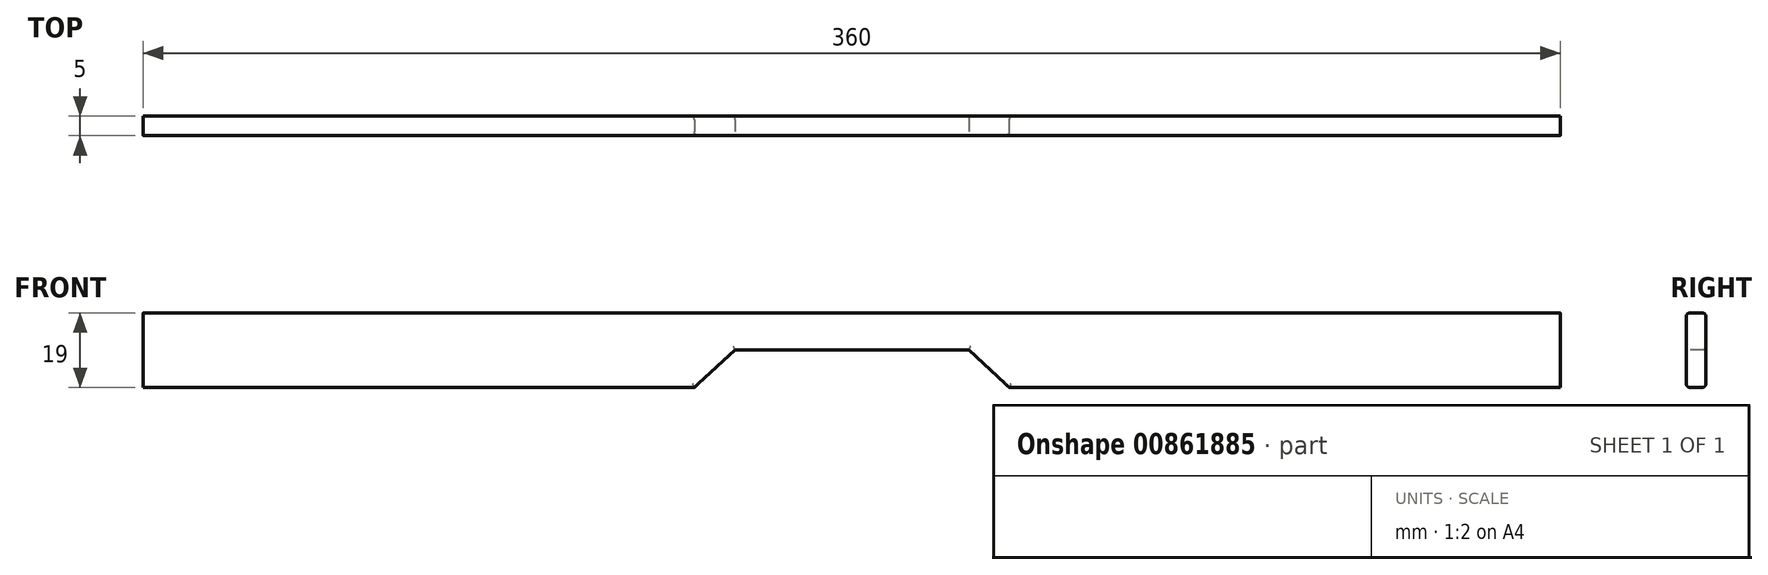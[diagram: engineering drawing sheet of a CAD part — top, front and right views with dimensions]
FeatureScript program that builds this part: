
annotation { "Feature Type Name" : "Feature", "Feature Type Description" : "" }
export const myFeature = defineFeature(function(context is Context, id is Id, definition is map)
    precondition{}
    {
        {
            var Q0;
            Q0=qCreatedBy(makeId("Front.planeOp"),FACE);
            var sketch = newSketch(context, id + "F0", { "sketchPlane" : qUnion([Q0])});
            skLineSegment(sketch, "E0.bottom", {"start": v(-180, 9.5) * mm, "end": v(180, 9.5) * mm});
            skLineSegment(sketch, "E0.top", {"start": v(-180, -9.5) * mm, "end": v(180, -9.5) * mm});
            skLineSegment(sketch, "E0.left", {"start": v(-180, 9.5) * mm, "end": v(-180, -9.5) * mm});
            skLineSegment(sketch, "E0.right", {"start": v(180, 9.5) * mm, "end": v(180, -9.5) * mm});
            skPoint(sketch, "E0.middle", {"position": v(0, 0) * mm});
            skSolve(sketch);
        }
        {
            var Q0;
            Q0=makeQuery(id+"F0.imprint","IMPRINT",FACE,{"disambiguationData":[TD([[makeQuery(id+"F0.imprint","IMPRINT",EDGE,{"derivedFrom":sQuery(id+"F0.wireOp",EDGE,"E0.bottom")}),-1.0]])]});
            extrude(context, id + "F1", {"entities" : qUnion([Q0]), "depth" : 5 * mm, "offsetDistance" : 25 * mm});
        }
        {
            var Q0;
            Q0=makeQuery(id+"F1.opExtrude","CAP_FACE",FACE,{"disambiguationData":[OSD([sQuery(id+"F0.wireOp",EDGE,"E0.bottom"),sQuery(id+"F0.wireOp",EDGE,"E0.top"),sQuery(id+"F0.wireOp",EDGE,"E0.left"),sQuery(id+"F0.wireOp",EDGE,"E0.right")])],"isStart":false});
            var sketch = newSketch(context, id + "F2", { "sketchPlane" : qUnion([Q0])});
            skLineSegment(sketch, "E1", {"start": v(-180, -9.5) * mm, "end": v(-40, -9.5) * mm});
            skLineSegment(sketch, "E2", {"start": v(180, -9.5) * mm, "end": v(40, -9.5) * mm});
            skLineSegment(sketch, "E3", {"start": v(-40, -9.5) * mm, "end": v(-29.72, 0) * mm});
            skLineSegment(sketch, "E4", {"start": v(-29.72, 0) * mm, "end": v(29.72, 0) * mm});
            skLineSegment(sketch, "E5", {"start": v(29.72, 0) * mm, "end": v(40, -9.5) * mm});
            skSolve(sketch);
        }
        {
            var Q0;
            Q0 = qSketchRegion(id + "F2", true);
            var Q1;
            {var subQ0=sQuery(id+"F2.wireOp",EDGE,"E3");Q1=makeQuery(id+"F2.imprint","IMPRINT",FACE,{"disambiguationData":[TD([[makeQuery(id+"F2.imprint","IMPRINT",EDGE,{"derivedFrom":subQ0}),-1.0]])]});}
            extrude(context, id + "F3", {"entities" : qUnion([Q0, Q1]), "operationType" : NewBodyOperationType.REMOVE, "oppositeDirection" : true, "depth" : 25 * mm, "offsetDistance" : 25 * mm});
        }
        {
            var Q0;
            Q0=makeQuery(id+"F1.opExtrude","CAP_EDGE",EDGE,{"disambiguationData":[OSD([sQuery(id+"F0.wireOp",EDGE,"E0.bottom")])],"isStart":false});
            var Q1;
            Q1=makeQuery(id+"F1.opExtrude","CAP_EDGE",EDGE,{"disambiguationData":[OSD([sQuery(id+"F0.wireOp",EDGE,"E0.bottom")])],"isStart":true});
            var Q2;
            {var subQ0=sQuery(id+"F0.wireOp",EDGE,"E0.left");var subQ1=sQuery(id+"F0.wireOp",EDGE,"E0.top");Q2=makeQuery(id+"F3.boolean.opBoolean","SPLIT",EDGE,{"disambiguationData":[TD([makeQuery(id+"F1.opExtrude","SWEPT_FACE",FACE,{"disambiguationData":[OSD([subQ0])]})])],"derivedFrom":makeQuery(id+"F1.opExtrude","CAP_EDGE",EDGE,{"disambiguationData":[OSD([subQ1])],"isStart":false})});}
            var Q3;
            {var subQ0=sQuery(id+"F0.wireOp",EDGE,"E0.right");var subQ1=sQuery(id+"F0.wireOp",EDGE,"E0.top");Q3=makeQuery(id+"F3.boolean.opBoolean","SPLIT",EDGE,{"disambiguationData":[TD([makeQuery(id+"F1.opExtrude","SWEPT_FACE",FACE,{"disambiguationData":[OSD([subQ0])]})])],"derivedFrom":makeQuery(id+"F1.opExtrude","CAP_EDGE",EDGE,{"disambiguationData":[OSD([subQ1])],"isStart":false})});}
            var Q4;
            Q4=makeQuery(id+"F3.boolean.opBoolean","COPY",EDGE,{"derivedFrom":makeQuery(id+"F3.opExtrude","CAP_EDGE",EDGE,{"disambiguationData":[OSD([sQuery(id+"F2.wireOp",EDGE,"E4")])],"isStart":true})});
            var Q5;
            Q5=makeQuery(id+"F3.boolean.opBoolean","COPY",EDGE,{"derivedFrom":makeQuery(id+"F3.opExtrude","CAP_EDGE",EDGE,{"disambiguationData":[OSD([sQuery(id+"F2.wireOp",EDGE,"E5")])],"isStart":true})});
            var Q6;
            Q6=makeQuery(id+"F3.boolean.opBoolean","COPY",EDGE,{"derivedFrom":makeQuery(id+"F3.opExtrude","CAP_EDGE",EDGE,{"disambiguationData":[OSD([sQuery(id+"F2.wireOp",EDGE,"E3")])],"isStart":true})});
            var Q7;
            {var subQ0=sQuery(id+"F0.wireOp",EDGE,"E0.left");var subQ1=sQuery(id+"F0.wireOp",EDGE,"E0.top");Q7=makeQuery(id+"F3.boolean.opBoolean","SPLIT",EDGE,{"disambiguationData":[TD([makeQuery(id+"F1.opExtrude","SWEPT_FACE",FACE,{"disambiguationData":[OSD([subQ0])]})])],"derivedFrom":makeQuery(id+"F1.opExtrude","CAP_EDGE",EDGE,{"disambiguationData":[OSD([subQ1])],"isStart":true})});}
            var Q8;
            Q8=makeQuery(id+"F3.boolean.opBoolean","INTERSECT",EDGE,{"derivedFrom":[makeQuery(id+"F1.opExtrude","CAP_FACE",FACE,{"disambiguationData":[OSD([sQuery(id+"F0.wireOp",EDGE,"E0.bottom"),sQuery(id+"F0.wireOp",EDGE,"E0.top"),sQuery(id+"F0.wireOp",EDGE,"E0.left"),sQuery(id+"F0.wireOp",EDGE,"E0.right")])],"isStart":true}),makeQuery(id+"F3.opExtrude","SWEPT_FACE",FACE,{"disambiguationData":[OSD([sQuery(id+"F2.wireOp",EDGE,"E4")])]})]});
            var Q9;
            Q9=makeQuery(id+"F3.boolean.opBoolean","INTERSECT",EDGE,{"derivedFrom":[makeQuery(id+"F1.opExtrude","CAP_FACE",FACE,{"disambiguationData":[OSD([sQuery(id+"F0.wireOp",EDGE,"E0.bottom"),sQuery(id+"F0.wireOp",EDGE,"E0.top"),sQuery(id+"F0.wireOp",EDGE,"E0.left"),sQuery(id+"F0.wireOp",EDGE,"E0.right")])],"isStart":true}),makeQuery(id+"F3.opExtrude","SWEPT_FACE",FACE,{"disambiguationData":[OSD([sQuery(id+"F2.wireOp",EDGE,"E3")])]})]});
            var Q10;
            Q10=makeQuery(id+"F3.boolean.opBoolean","INTERSECT",EDGE,{"derivedFrom":[makeQuery(id+"F1.opExtrude","CAP_FACE",FACE,{"disambiguationData":[OSD([sQuery(id+"F0.wireOp",EDGE,"E0.bottom"),sQuery(id+"F0.wireOp",EDGE,"E0.top"),sQuery(id+"F0.wireOp",EDGE,"E0.left"),sQuery(id+"F0.wireOp",EDGE,"E0.right")])],"isStart":true}),makeQuery(id+"F3.opExtrude","SWEPT_FACE",FACE,{"disambiguationData":[OSD([sQuery(id+"F2.wireOp",EDGE,"E5")])]})]});
            var Q11;
            {var subQ0=sQuery(id+"F0.wireOp",EDGE,"E0.right");var subQ1=sQuery(id+"F0.wireOp",EDGE,"E0.top");Q11=makeQuery(id+"F3.boolean.opBoolean","SPLIT",EDGE,{"disambiguationData":[TD([makeQuery(id+"F1.opExtrude","SWEPT_FACE",FACE,{"disambiguationData":[OSD([subQ0])]})])],"derivedFrom":makeQuery(id+"F1.opExtrude","CAP_EDGE",EDGE,{"disambiguationData":[OSD([subQ1])],"isStart":true})});}
            fillet(context, id + "F4", {"entities" : qUnion([Q0, Q1, Q2, Q3, Q4, Q5, Q6, Q7, Q8, Q9, Q10, Q11]), "radius" : 1 * mm, "tangentPropagation" : true, "allowEdgeOverflow" : false});
        }
    });
